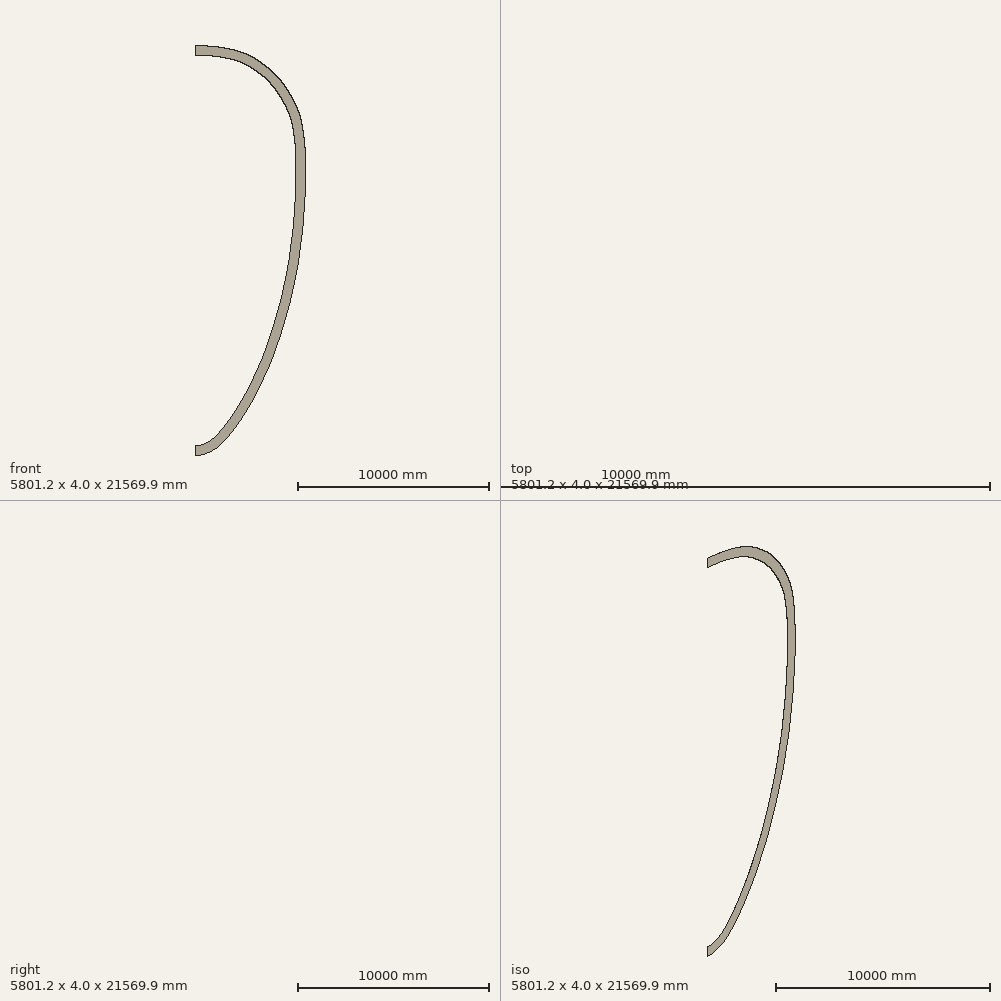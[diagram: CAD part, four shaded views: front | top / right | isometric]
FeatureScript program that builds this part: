
annotation { "Feature Type Name" : "Feature", "Feature Type Description" : "" }
export const myFeature = defineFeature(function(context is Context, id is Id, definition is map)
    precondition{}
    {
        {
            var Q0;
            Q0=qCreatedBy(makeId("Front.planeOp"),FACE);
            var sketch = newSketch(context, id + "F0", { "sketchPlane" : qUnion([Q0])});
            skLineSegment(sketch, "E0", {"start": v(-2899.69, 10773.69) * mm, "end": v(-2864.08, 10778.08) * mm});
            skLineSegment(sketch, "E1", {"start": v(-2864.08, 10778.08) * mm, "end": v(-2743.96, 10784.97) * mm});
            skLineSegment(sketch, "E2", {"start": v(-2743.96, 10784.97) * mm, "end": v(-2600.66, 10781.18) * mm});
            skLineSegment(sketch, "E3", {"start": v(-2600.66, 10781.18) * mm, "end": v(-2482.22, 10772.55) * mm});
            skLineSegment(sketch, "E4", {"start": v(-2482.22, 10772.55) * mm, "end": v(-2197.18, 10755.78) * mm});
            skLineSegment(sketch, "E5", {"start": v(-2197.18, 10755.78) * mm, "end": v(-1894.64, 10734.17) * mm});
            skLineSegment(sketch, "E6", {"start": v(-1894.64, 10734.17) * mm, "end": v(-1613.79, 10697.74) * mm});
            skLineSegment(sketch, "E7", {"start": v(-1613.79, 10697.74) * mm, "end": v(-1345.7, 10651.6) * mm});
            skLineSegment(sketch, "E8", {"start": v(-1345.7, 10651.6) * mm, "end": v(-1296.64, 10642.52) * mm});
            skLineSegment(sketch, "E9", {"start": v(-1296.64, 10642.52) * mm, "end": v(-962.28, 10574.07) * mm});
            skLineSegment(sketch, "E10", {"start": v(-962.28, 10574.07) * mm, "end": v(-784.35, 10530.15) * mm});
            skLineSegment(sketch, "E11", {"start": v(-784.35, 10530.15) * mm, "end": v(-601.1, 10477.25) * mm});
            skLineSegment(sketch, "E12", {"start": v(-601.1, 10477.25) * mm, "end": v(-432.33, 10419.92) * mm});
            skLineSegment(sketch, "E13", {"start": v(-432.33, 10419.92) * mm, "end": v(-266.34, 10354.84) * mm});
            skLineSegment(sketch, "E14", {"start": v(-266.34, 10354.84) * mm, "end": v(-102.26, 10281.62) * mm});
            skLineSegment(sketch, "E15", {"start": v(-102.26, 10281.62) * mm, "end": v(58.32, 10201) * mm});
            skLineSegment(sketch, "E16", {"start": v(58.32, 10201) * mm, "end": v(293.67, 10065.46) * mm});
            skLineSegment(sketch, "E17", {"start": v(293.67, 10065.46) * mm, "end": v(512.78, 9917.58) * mm});
            skLineSegment(sketch, "E18", {"start": v(512.78, 9917.58) * mm, "end": v(640.94, 9820.83) * mm});
            skLineSegment(sketch, "E19", {"start": v(640.94, 9820.83) * mm, "end": v(752.86, 9736.4) * mm});
            skLineSegment(sketch, "E20", {"start": v(752.86, 9736.4) * mm, "end": v(865.96, 9655.84) * mm});
            skLineSegment(sketch, "E21", {"start": v(865.96, 9655.84) * mm, "end": v(996.26, 9558.5) * mm});
            skLineSegment(sketch, "E22", {"start": v(996.26, 9558.5) * mm, "end": v(1102.74, 9467.34) * mm});
            skLineSegment(sketch, "E23", {"start": v(1102.74, 9467.34) * mm, "end": v(1192.12, 9382.4) * mm});
            skLineSegment(sketch, "E24", {"start": v(1192.12, 9382.4) * mm, "end": v(1104.65, 9290.35) * mm});
            skLineSegment(sketch, "E25", {"start": v(1104.65, 9290.35) * mm, "end": v(1192.12, 9382.4) * mm});
            skLineSegment(sketch, "E26", {"start": v(1192.12, 9382.4) * mm, "end": v(1216.23, 9358.22) * mm});
            skLineSegment(sketch, "E27", {"start": v(1216.23, 9358.22) * mm, "end": v(1398.6, 9162.77) * mm});
            skLineSegment(sketch, "E28", {"start": v(1398.6, 9162.77) * mm, "end": v(1548.94, 8993.58) * mm});
            skLineSegment(sketch, "E29", {"start": v(1548.94, 8993.58) * mm, "end": v(1698.9, 8809.76) * mm});
            skLineSegment(sketch, "E30", {"start": v(1698.9, 8809.76) * mm, "end": v(1836.22, 8615.76) * mm});
            skLineSegment(sketch, "E31", {"start": v(1836.22, 8615.76) * mm, "end": v(1958.04, 8425.87) * mm});
            skLineSegment(sketch, "E32", {"start": v(1958.04, 8425.87) * mm, "end": v(2081.07, 8225.46) * mm});
            skLineSegment(sketch, "E33", {"start": v(2081.07, 8225.46) * mm, "end": v(2202.66, 8014.64) * mm});
            skLineSegment(sketch, "E34", {"start": v(2202.66, 8014.64) * mm, "end": v(2289.2, 7851.67) * mm});
            skLineSegment(sketch, "E35", {"start": v(2289.2, 7851.67) * mm, "end": v(2370.15, 7685.81) * mm});
            skLineSegment(sketch, "E36", {"start": v(2370.15, 7685.81) * mm, "end": v(2445.51, 7516.01) * mm});
            skLineSegment(sketch, "E37", {"start": v(2445.51, 7516.01) * mm, "end": v(2514.3, 7343.42) * mm});
            skLineSegment(sketch, "E38", {"start": v(2514.3, 7343.42) * mm, "end": v(2590.27, 7126.25) * mm});
            skLineSegment(sketch, "E39", {"start": v(2590.27, 7126.25) * mm, "end": v(2661.16, 6895.64) * mm});
            skLineSegment(sketch, "E40", {"start": v(2661.16, 6895.64) * mm, "end": v(2539.77, 6858.33) * mm});
            skLineSegment(sketch, "E41", {"start": v(2539.77, 6858.33) * mm, "end": v(2661.16, 6895.64) * mm});
            skLineSegment(sketch, "E42", {"start": v(2661.16, 6895.64) * mm, "end": v(2708.12, 6653.76) * mm});
            skLineSegment(sketch, "E43", {"start": v(2708.12, 6653.76) * mm, "end": v(2759.46, 6353.63) * mm});
            skLineSegment(sketch, "E44", {"start": v(2759.46, 6353.63) * mm, "end": v(2803.5, 6051) * mm});
            skLineSegment(sketch, "E45", {"start": v(2803.5, 6051) * mm, "end": v(2843.56, 5710.28) * mm});
            skLineSegment(sketch, "E46", {"start": v(2843.56, 5710.28) * mm, "end": v(2870.73, 5364.25) * mm});
            skLineSegment(sketch, "E47", {"start": v(2870.73, 5364.25) * mm, "end": v(2882.87, 5013) * mm});
            skLineSegment(sketch, "E48", {"start": v(2882.87, 5013) * mm, "end": v(2888.36, 4674.2) * mm});
            skLineSegment(sketch, "E49", {"start": v(2888.36, 4674.2) * mm, "end": v(2897.28, 4278.15) * mm});
            skLineSegment(sketch, "E50", {"start": v(2897.28, 4278.15) * mm, "end": v(2770.33, 4275.3) * mm});
            skLineSegment(sketch, "E51", {"start": v(2770.33, 4275.3) * mm, "end": v(2897.28, 4278.15) * mm});
            skLineSegment(sketch, "E52", {"start": v(2897.28, 4278.15) * mm, "end": v(2898.2, 4155.85) * mm});
            skLineSegment(sketch, "E53", {"start": v(2898.2, 4155.85) * mm, "end": v(2901.47, 3607.16) * mm});
            skLineSegment(sketch, "E54", {"start": v(2901.47, 3607.16) * mm, "end": v(2889.22, 3149.3) * mm});
            skLineSegment(sketch, "E55", {"start": v(2889.22, 3149.3) * mm, "end": v(2850.08, 2494.33) * mm});
            skLineSegment(sketch, "E56", {"start": v(2850.08, 2494.33) * mm, "end": v(2811.53, 1938.1) * mm});
            skLineSegment(sketch, "E57", {"start": v(2811.53, 1938.1) * mm, "end": v(2767.89, 1286.2) * mm});
            skLineSegment(sketch, "E58", {"start": v(2767.89, 1286.2) * mm, "end": v(2641.17, 1294.69) * mm});
            skLineSegment(sketch, "E59", {"start": v(2641.17, 1294.69) * mm, "end": v(2767.89, 1286.2) * mm});
            skLineSegment(sketch, "E60", {"start": v(2767.89, 1286.2) * mm, "end": v(2707.3, 762.86) * mm});
            skLineSegment(sketch, "E61", {"start": v(2707.3, 762.86) * mm, "end": v(2649.45, 362.86) * mm});
            skLineSegment(sketch, "E62", {"start": v(2649.45, 362.86) * mm, "end": v(2595.6, -80.54) * mm});
            skLineSegment(sketch, "E63", {"start": v(2595.6, -80.54) * mm, "end": v(2536.93, -541.58) * mm});
            skLineSegment(sketch, "E64", {"start": v(2536.93, -541.58) * mm, "end": v(2492.96, -808.33) * mm});
            skLineSegment(sketch, "E65", {"start": v(2492.96, -808.33) * mm, "end": v(2442.46, -1073.96) * mm});
            skLineSegment(sketch, "E66", {"start": v(2442.46, -1073.96) * mm, "end": v(2335.6, -1591.59) * mm});
            skLineSegment(sketch, "E67", {"start": v(2335.6, -1591.59) * mm, "end": v(2219.96, -2155.37) * mm});
            skLineSegment(sketch, "E68", {"start": v(2219.96, -2155.37) * mm, "end": v(2157.65, -2441.5) * mm});
            skLineSegment(sketch, "E69", {"start": v(2157.65, -2441.5) * mm, "end": v(2089.56, -2726.26) * mm});
            skLineSegment(sketch, "E70", {"start": v(2089.56, -2726.26) * mm, "end": v(1979.55, -3131.29) * mm});
            skLineSegment(sketch, "E71", {"start": v(1979.55, -3131.29) * mm, "end": v(1865.22, -3524.73) * mm});
            skLineSegment(sketch, "E72", {"start": v(1865.22, -3524.73) * mm, "end": v(1739.8, -3955.87) * mm});
            skLineSegment(sketch, "E73", {"start": v(1739.8, -3955.87) * mm, "end": v(1606.6, -4391.03) * mm});
            skLineSegment(sketch, "E74", {"start": v(1606.6, -4391.03) * mm, "end": v(1497.97, -4716.55) * mm});
            skLineSegment(sketch, "E75", {"start": v(1497.97, -4716.55) * mm, "end": v(1388.03, -5035.45) * mm});
            skLineSegment(sketch, "E76", {"start": v(1388.03, -5035.45) * mm, "end": v(1237.18, -5471.36) * mm});
            skLineSegment(sketch, "E77", {"start": v(1237.18, -5471.36) * mm, "end": v(1155.88, -5693.84) * mm});
            skLineSegment(sketch, "E78", {"start": v(1155.88, -5693.84) * mm, "end": v(1069.14, -5914.19) * mm});
            skLineSegment(sketch, "E79", {"start": v(1069.14, -5914.19) * mm, "end": v(896.01, -6307.56) * mm});
            skLineSegment(sketch, "E80", {"start": v(896.01, -6307.56) * mm, "end": v(721.33, -6683.93) * mm});
            skLineSegment(sketch, "E81", {"start": v(721.33, -6683.93) * mm, "end": v(498.5, -7174.56) * mm});
            skLineSegment(sketch, "E82", {"start": v(498.5, -7174.56) * mm, "end": v(379.12, -7425.64) * mm});
            skLineSegment(sketch, "E83", {"start": v(379.12, -7425.64) * mm, "end": v(251.64, -7672.58) * mm});
            skLineSegment(sketch, "E84", {"start": v(251.64, -7672.58) * mm, "end": v(36.73, -8045.96) * mm});
            skLineSegment(sketch, "E85", {"start": v(36.73, -8045.96) * mm, "end": v(-141.9, -8348.93) * mm});
            skLineSegment(sketch, "E86", {"start": v(-141.9, -8348.93) * mm, "end": v(-326.6, -8653.5) * mm});
            skLineSegment(sketch, "E87", {"start": v(-326.6, -8653.5) * mm, "end": v(-526.03, -8962.42) * mm});
            skLineSegment(sketch, "E88", {"start": v(-526.03, -8962.42) * mm, "end": v(-738.56, -9266.68) * mm});
            skLineSegment(sketch, "E89", {"start": v(-738.56, -9266.68) * mm, "end": v(-983.74, -9587.59) * mm});
            skLineSegment(sketch, "E90", {"start": v(-983.74, -9587.59) * mm, "end": v(-1243.23, -9899.04) * mm});
            skLineSegment(sketch, "E91", {"start": v(-1243.23, -9899.04) * mm, "end": v(-1450.09, -10125.79) * mm});
            skLineSegment(sketch, "E92", {"start": v(-1450.09, -10125.79) * mm, "end": v(-1570.4, -10241.43) * mm});
            skLineSegment(sketch, "E93", {"start": v(-1570.4, -10241.43) * mm, "end": v(-1698.35, -10348.5) * mm});
            skLineSegment(sketch, "E94", {"start": v(-1698.35, -10348.5) * mm, "end": v(-1835.18, -10445.27) * mm});
            skLineSegment(sketch, "E95", {"start": v(-1835.18, -10445.27) * mm, "end": v(-1979.24, -10531.1) * mm});
            skLineSegment(sketch, "E96", {"start": v(-1979.24, -10531.1) * mm, "end": v(-2122.25, -10603.2) * mm});
            skLineSegment(sketch, "E97", {"start": v(-2122.25, -10603.2) * mm, "end": v(-2269.44, -10666.22) * mm});
            skLineSegment(sketch, "E98", {"start": v(-2269.44, -10666.22) * mm, "end": v(-2412.21, -10717.35) * mm});
            skLineSegment(sketch, "E99", {"start": v(-2412.21, -10717.35) * mm, "end": v(-2565.96, -10758) * mm});
            skLineSegment(sketch, "E100", {"start": v(-2565.96, -10758) * mm, "end": v(-2656.3, -10773.49) * mm});
            skLineSegment(sketch, "E101", {"start": v(-2656.3, -10773.49) * mm, "end": v(-2747.52, -10782.86) * mm});
            skLineSegment(sketch, "E102", {"start": v(-2747.52, -10782.86) * mm, "end": v(-2899.69, -10784.97) * mm});
            skLineSegment(sketch, "E103", {"start": v(-2899.69, -10784.97) * mm, "end": v(-2901.47, -10658) * mm});
            skLineSegment(sketch, "E104", {"start": v(-2901.47, -10658) * mm, "end": v(-2899.69, -10784.97) * mm});
            skLineSegment(sketch, "E105", {"start": v(-2899.69, -10784.97) * mm, "end": v(-2899.69, -10277.02) * mm});
            skLineSegment(sketch, "E106", {"start": v(-2899.69, -10277.02) * mm, "end": v(-2772.69, -10277.02) * mm});
            skLineSegment(sketch, "E107", {"start": v(-2772.69, -10277.02) * mm, "end": v(-2899.69, -10277.02) * mm});
            skLineSegment(sketch, "E108", {"start": v(-2899.69, -10277.02) * mm, "end": v(-2778.76, -10275.32) * mm});
            skLineSegment(sketch, "E109", {"start": v(-2778.76, -10275.32) * mm, "end": v(-2659, -10258.9) * mm});
            skLineSegment(sketch, "E110", {"start": v(-2659, -10258.9) * mm, "end": v(-2556.51, -10231.8) * mm});
            skLineSegment(sketch, "E111", {"start": v(-2556.51, -10231.8) * mm, "end": v(-2456.36, -10195.92) * mm});
            skLineSegment(sketch, "E112", {"start": v(-2456.36, -10195.92) * mm, "end": v(-2220.11, -10085.83) * mm});
            skLineSegment(sketch, "E113", {"start": v(-2220.11, -10085.83) * mm, "end": v(-2002.54, -9944.35) * mm});
            skLineSegment(sketch, "E114", {"start": v(-2002.54, -9944.35) * mm, "end": v(-1802.87, -9765.16) * mm});
            skLineSegment(sketch, "E115", {"start": v(-1802.87, -9765.16) * mm, "end": v(-1621.1, -9565.87) * mm});
            skLineSegment(sketch, "E116", {"start": v(-1621.1, -9565.87) * mm, "end": v(-1376.12, -9271.69) * mm});
            skLineSegment(sketch, "E117", {"start": v(-1376.12, -9271.69) * mm, "end": v(-1144.32, -8968.23) * mm});
            skLineSegment(sketch, "E118", {"start": v(-1144.32, -8968.23) * mm, "end": v(-943.58, -8680.75) * mm});
            skLineSegment(sketch, "E119", {"start": v(-943.58, -8680.75) * mm, "end": v(-753.34, -8385.96) * mm});
            skLineSegment(sketch, "E120", {"start": v(-753.34, -8385.96) * mm, "end": v(-574.27, -8090.48) * mm});
            skLineSegment(sketch, "E121", {"start": v(-574.27, -8090.48) * mm, "end": v(-398.8, -7792.82) * mm});
            skLineSegment(sketch, "E122", {"start": v(-398.8, -7792.82) * mm, "end": v(-193.4, -7435.8) * mm});
            skLineSegment(sketch, "E123", {"start": v(-193.4, -7435.8) * mm, "end": v(42.32, -6960.1) * mm});
            skLineSegment(sketch, "E124", {"start": v(42.32, -6960.1) * mm, "end": v(262.1, -6475.9) * mm});
            skLineSegment(sketch, "E125", {"start": v(262.1, -6475.9) * mm, "end": v(435.28, -6102.6) * mm});
            skLineSegment(sketch, "E126", {"start": v(435.28, -6102.6) * mm, "end": v(600.79, -5726.4) * mm});
            skLineSegment(sketch, "E127", {"start": v(600.79, -5726.4) * mm, "end": v(761.24, -5303.34) * mm});
            skLineSegment(sketch, "E128", {"start": v(761.24, -5303.34) * mm, "end": v(909.3, -4875.25) * mm});
            skLineSegment(sketch, "E129", {"start": v(909.3, -4875.25) * mm, "end": v(1018.16, -4559.35) * mm});
            skLineSegment(sketch, "E130", {"start": v(1018.16, -4559.35) * mm, "end": v(1123.8, -4242.56) * mm});
            skLineSegment(sketch, "E131", {"start": v(1123.8, -4242.56) * mm, "end": v(1253.9, -3817.34) * mm});
            skLineSegment(sketch, "E132", {"start": v(1253.9, -3817.34) * mm, "end": v(1378.08, -3390.14) * mm});
            skLineSegment(sketch, "E133", {"start": v(1378.08, -3390.14) * mm, "end": v(1490.95, -3001.47) * mm});
            skLineSegment(sketch, "E134", {"start": v(1490.95, -3001.47) * mm, "end": v(1596.87, -2611.12) * mm});
            skLineSegment(sketch, "E135", {"start": v(1596.87, -2611.12) * mm, "end": v(1723.5, -2056.4) * mm});
            skLineSegment(sketch, "E136", {"start": v(1723.5, -2056.4) * mm, "end": v(1837.87, -1498.45) * mm});
            skLineSegment(sketch, "E137", {"start": v(1837.87, -1498.45) * mm, "end": v(1943.13, -988.03) * mm});
            skLineSegment(sketch, "E138", {"start": v(1943.13, -988.03) * mm, "end": v(2034, -475.44) * mm});
            skLineSegment(sketch, "E139", {"start": v(2034, -475.44) * mm, "end": v(2090.78, -28.73) * mm});
            skLineSegment(sketch, "E140", {"start": v(2090.78, -28.73) * mm, "end": v(2145, 418.52) * mm});
            skLineSegment(sketch, "E141", {"start": v(2145, 418.52) * mm, "end": v(2202.54, 816.66) * mm});
            skLineSegment(sketch, "E142", {"start": v(2202.54, 816.66) * mm, "end": v(2262.12, 1332.28) * mm});
            skLineSegment(sketch, "E143", {"start": v(2262.12, 1332.28) * mm, "end": v(2388.29, 1317.7) * mm});
            skLineSegment(sketch, "E144", {"start": v(2388.29, 1317.7) * mm, "end": v(2262.12, 1332.28) * mm});
            skLineSegment(sketch, "E145", {"start": v(2262.12, 1332.28) * mm, "end": v(2305.5, 1982.11) * mm});
            skLineSegment(sketch, "E146", {"start": v(2305.5, 1982.11) * mm, "end": v(2343.68, 2534.26) * mm});
            skLineSegment(sketch, "E147", {"start": v(2343.68, 2534.26) * mm, "end": v(2381.86, 3175.79) * mm});
            skLineSegment(sketch, "E148", {"start": v(2381.86, 3175.79) * mm, "end": v(2393.54, 3615.1) * mm});
            skLineSegment(sketch, "E149", {"start": v(2393.54, 3615.1) * mm, "end": v(2390.22, 4152.95) * mm});
            skLineSegment(sketch, "E150", {"start": v(2390.22, 4152.95) * mm, "end": v(2389.35, 4270.6) * mm});
            skLineSegment(sketch, "E151", {"start": v(2389.35, 4270.6) * mm, "end": v(2516.35, 4271.52) * mm});
            skLineSegment(sketch, "E152", {"start": v(2516.35, 4271.52) * mm, "end": v(2389.35, 4270.6) * mm});
            skLineSegment(sketch, "E153", {"start": v(2389.35, 4270.6) * mm, "end": v(2380.46, 4664.33) * mm});
            skLineSegment(sketch, "E154", {"start": v(2380.46, 4664.33) * mm, "end": v(2375, 5000.12) * mm});
            skLineSegment(sketch, "E155", {"start": v(2375, 5000.12) * mm, "end": v(2363.42, 5335.57) * mm});
            skLineSegment(sketch, "E156", {"start": v(2363.42, 5335.57) * mm, "end": v(2337.9, 5660.7) * mm});
            skLineSegment(sketch, "E157", {"start": v(2337.9, 5660.7) * mm, "end": v(2299.77, 5984.75) * mm});
            skLineSegment(sketch, "E158", {"start": v(2299.77, 5984.75) * mm, "end": v(2257.65, 6274.23) * mm});
            skLineSegment(sketch, "E159", {"start": v(2257.65, 6274.23) * mm, "end": v(2208.33, 6562.52) * mm});
            skLineSegment(sketch, "E160", {"start": v(2208.33, 6562.52) * mm, "end": v(2167.61, 6772.4) * mm});
            skLineSegment(sketch, "E161", {"start": v(2167.61, 6772.4) * mm, "end": v(2292.27, 6796.6) * mm});
            skLineSegment(sketch, "E162", {"start": v(2292.27, 6796.6) * mm, "end": v(2167.61, 6772.4) * mm});
            skLineSegment(sketch, "E163", {"start": v(2167.61, 6772.4) * mm, "end": v(2107.8, 6967.47) * mm});
            skLineSegment(sketch, "E164", {"start": v(2107.8, 6967.47) * mm, "end": v(2040.53, 7160.1) * mm});
            skLineSegment(sketch, "E165", {"start": v(2040.53, 7160.1) * mm, "end": v(1910.2, 7470.27) * mm});
            skLineSegment(sketch, "E166", {"start": v(1910.2, 7470.27) * mm, "end": v(1757.68, 7770.22) * mm});
            skLineSegment(sketch, "E167", {"start": v(1757.68, 7770.22) * mm, "end": v(1646.6, 7963.03) * mm});
            skLineSegment(sketch, "E168", {"start": v(1646.6, 7963.03) * mm, "end": v(1530.27, 8152.84) * mm});
            skLineSegment(sketch, "E169", {"start": v(1530.27, 8152.84) * mm, "end": v(1417.85, 8328.36) * mm});
            skLineSegment(sketch, "E170", {"start": v(1417.85, 8328.36) * mm, "end": v(1297.71, 8498.3) * mm});
            skLineSegment(sketch, "E171", {"start": v(1297.71, 8498.3) * mm, "end": v(1165.96, 8660.05) * mm});
            skLineSegment(sketch, "E172", {"start": v(1165.96, 8660.05) * mm, "end": v(1027.3, 8816.29) * mm});
            skLineSegment(sketch, "E173", {"start": v(1027.3, 8816.29) * mm, "end": v(855.4, 9000.74) * mm});
            skLineSegment(sketch, "E174", {"start": v(855.4, 9000.74) * mm, "end": v(837.26, 9018.98) * mm});
            skLineSegment(sketch, "E175", {"start": v(837.26, 9018.98) * mm, "end": v(927.28, 9108.57) * mm});
            skLineSegment(sketch, "E176", {"start": v(927.28, 9108.57) * mm, "end": v(837.26, 9018.98) * mm});
            skLineSegment(sketch, "E177", {"start": v(837.26, 9018.98) * mm, "end": v(757.5, 9094.65) * mm});
            skLineSegment(sketch, "E178", {"start": v(757.5, 9094.65) * mm, "end": v(673.96, 9166.07) * mm});
            skLineSegment(sketch, "E179", {"start": v(673.96, 9166.07) * mm, "end": v(561.92, 9249.64) * mm});
            skLineSegment(sketch, "E180", {"start": v(561.92, 9249.64) * mm, "end": v(447.93, 9330.72) * mm});
            skLineSegment(sketch, "E181", {"start": v(447.93, 9330.72) * mm, "end": v(330.58, 9419.13) * mm});
            skLineSegment(sketch, "E182", {"start": v(330.58, 9419.13) * mm, "end": v(213.23, 9507.55) * mm});
            skLineSegment(sketch, "E183", {"start": v(213.23, 9507.55) * mm, "end": v(20.42, 9637.47) * mm});
            skLineSegment(sketch, "E184", {"start": v(20.42, 9637.47) * mm, "end": v(-181.3, 9753.47) * mm});
            skLineSegment(sketch, "E185", {"start": v(-181.3, 9753.47) * mm, "end": v(-466.12, 9888.17) * mm});
            skLineSegment(sketch, "E186", {"start": v(-466.12, 9888.17) * mm, "end": v(-761.9, 9996.07) * mm});
            skLineSegment(sketch, "E187", {"start": v(-761.9, 9996.07) * mm, "end": v(-918.41, 10041.15) * mm});
            skLineSegment(sketch, "E188", {"start": v(-918.41, 10041.15) * mm, "end": v(-1076.55, 10080.04) * mm});
            skLineSegment(sketch, "E189", {"start": v(-1076.55, 10080.04) * mm, "end": v(-1395.86, 10145.17) * mm});
            skLineSegment(sketch, "E190", {"start": v(-1395.86, 10145.17) * mm, "end": v(-1436.95, 10152.76) * mm});
            skLineSegment(sketch, "E191", {"start": v(-1436.95, 10152.76) * mm, "end": v(-1691.08, 10196.3) * mm});
            skLineSegment(sketch, "E192", {"start": v(-1691.08, 10196.3) * mm, "end": v(-1946.58, 10229.24) * mm});
            skLineSegment(sketch, "E193", {"start": v(-1946.58, 10229.24) * mm, "end": v(-2230.88, 10249.36) * mm});
            skLineSegment(sketch, "E194", {"start": v(-2230.88, 10249.36) * mm, "end": v(-2515.84, 10265.92) * mm});
            skLineSegment(sketch, "E195", {"start": v(-2515.84, 10265.92) * mm, "end": v(-2625.93, 10273.84) * mm});
            skLineSegment(sketch, "E196", {"start": v(-2625.93, 10273.84) * mm, "end": v(-2736.06, 10276.69) * mm});
            skLineSegment(sketch, "E197", {"start": v(-2736.06, 10276.69) * mm, "end": v(-2818.08, 10271.91) * mm});
            skLineSegment(sketch, "E198", {"start": v(-2818.08, 10271.91) * mm, "end": v(-2899.69, 10261.83) * mm});
            skLineSegment(sketch, "E199", {"start": v(-2899.69, 10261.83) * mm, "end": v(-2899.69, 10388.83) * mm});
            skLineSegment(sketch, "E200", {"start": v(-2899.69, 10388.83) * mm, "end": v(-2899.69, 10261.83) * mm});
            skLineSegment(sketch, "E201", {"start": v(-2899.69, 10261.83) * mm, "end": v(-2899.69, 10773.69) * mm});
            skSolve(sketch);
        }
        {
            var Q0;
            Q0 = qSketchRegion(id + "F0", true);
            extrude(context, id + "F1", {"entities" : qUnion([Q0]), "depth" : 4 * mm, "offsetDistance" : 25 * mm});
        }
    });
